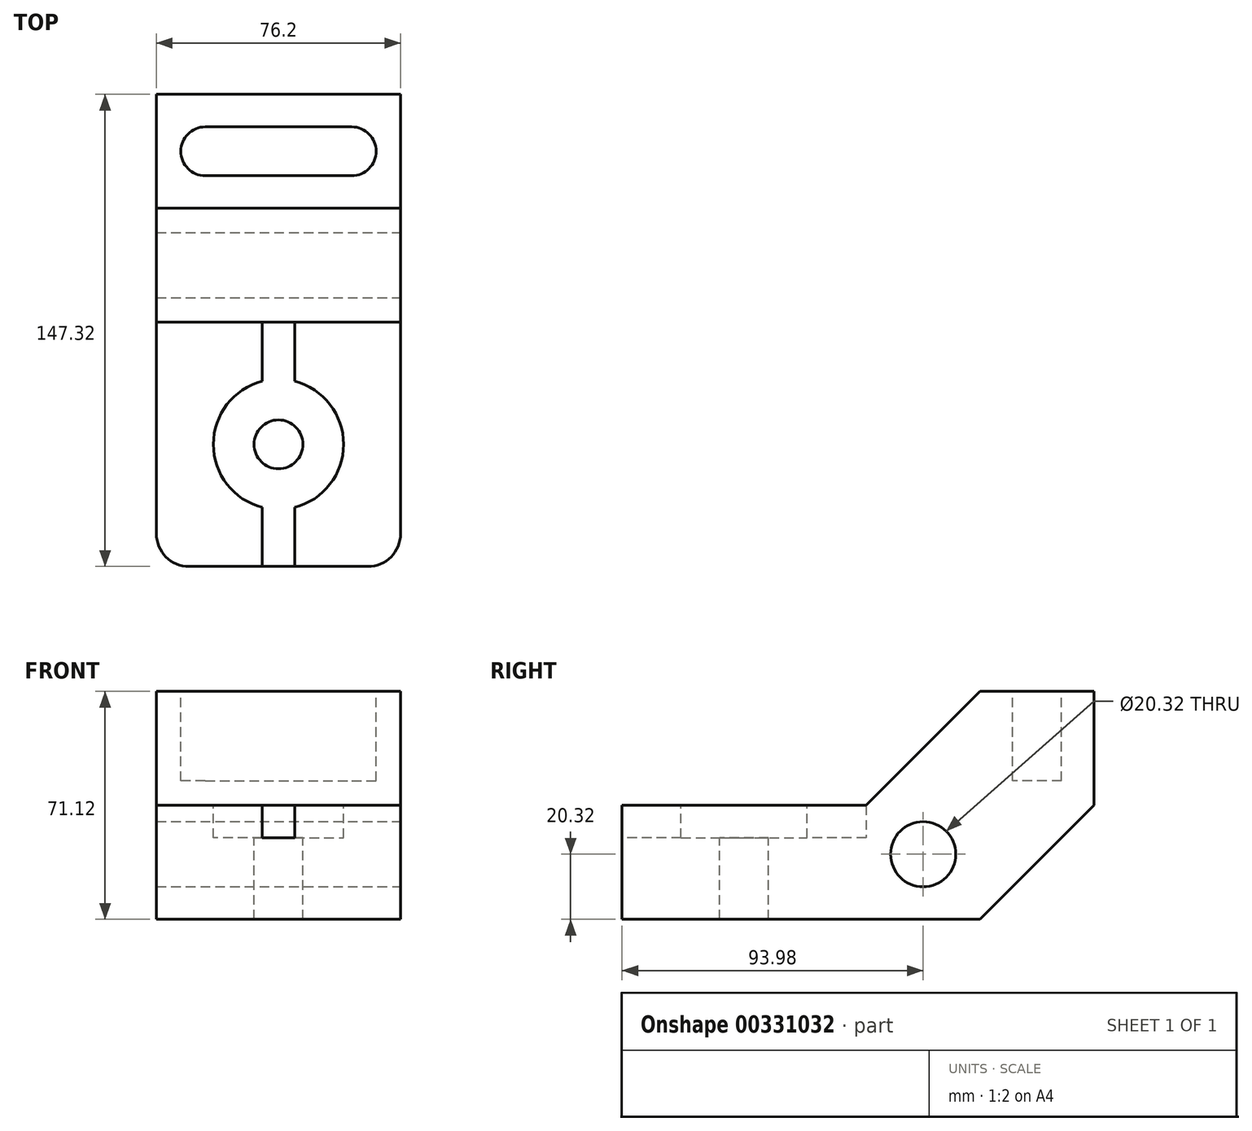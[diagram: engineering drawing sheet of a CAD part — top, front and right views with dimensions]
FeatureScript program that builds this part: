
annotation { "Feature Type Name" : "Feature", "Feature Type Description" : "" }
export const myFeature = defineFeature(function(context is Context, id is Id, definition is map)
    precondition{}
    {
        {
            var Q0;
            Q0=qCreatedBy(makeId("Right.planeOp"),FACE);
            var sketch = newSketch(context, id + "F0", { "sketchPlane" : qUnion([Q0])});
            skLineSegment(sketch, "E0", {"start": v(0, 0) * mm, "end": v(0, 35.56) * mm});
            skLineSegment(sketch, "E1", {"start": v(0, 35.56) * mm, "end": v(76.2, 35.56) * mm});
            skLineSegment(sketch, "E2", {"start": v(76.2, 35.56) * mm, "end": v(111.76, 71.12) * mm});
            skLineSegment(sketch, "E3", {"start": v(111.76, 71.12) * mm, "end": v(147.32, 71.12) * mm});
            skLineSegment(sketch, "E4", {"start": v(147.32, 71.12) * mm, "end": v(147.32, 35.56) * mm});
            skLineSegment(sketch, "E5", {"start": v(147.32, 35.56) * mm, "end": v(111.76, 0) * mm});
            skLineSegment(sketch, "E6", {"start": v(111.76, 0) * mm, "end": v(0, 0) * mm});
            skSolve(sketch);
        }
        {
            var Q0;
            Q0 = qSketchRegion(id + "F0", true);
            extrude(context, id + "F1", {"entities" : qUnion([Q0]), "depth" : 76.2 * mm});
        }
        {
            var Q0;
            Q0=makeQuery(id+"F1.opExtrude","SWEPT_FACE",FACE,{"disambiguationData":[OSD([sQuery(id+"F0.wireOp",EDGE,"E3")])]});
            var sketch = newSketch(context, id + "F2", { "sketchPlane" : qUnion([Q0])});
            skLineSegment(sketch, "E7", {"start": v(15.24, 129.54) * mm, "end": v(60.96, 129.54) * mm, "construction": true});
            skArc(sketch, "E8.0.startCap", {"start": v(15.24, 121.92) * mm, "mid": v(7.62, 129.54) * mm, "end": v(15.24, 137.16) * mm});
            skArc(sketch, "E8.0.endCap", {"start": v(60.96, 137.16) * mm, "mid": v(68.58, 129.54) * mm, "end": v(60.96, 121.92) * mm});
            skLineSegment(sketch, "E8.0.left", {"start": v(15.24, 137.16) * mm, "end": v(60.96, 137.16) * mm});
            skLineSegment(sketch, "E8.0.right", {"start": v(15.24, 121.92) * mm, "end": v(60.96, 121.92) * mm});
            skSolve(sketch);
        }
        {
            var Q0;
            Q0 = qSketchRegion(id + "F2", true);
            extrude(context, id + "F3", {"entities" : qUnion([Q0]), "operationType" : NewBodyOperationType.REMOVE, "oppositeDirection" : true, "depth" : 27.94 * mm});
        }
        {
            var Q0;
            Q0=makeQuery(id+"F1.opExtrude","CAP_FACE",FACE,{"disambiguationData":[OSD([sQuery(id+"F0.wireOp",EDGE,"E0"),sQuery(id+"F0.wireOp",EDGE,"E1"),sQuery(id+"F0.wireOp",EDGE,"E2"),sQuery(id+"F0.wireOp",EDGE,"E3"),sQuery(id+"F0.wireOp",EDGE,"E4"),sQuery(id+"F0.wireOp",EDGE,"E5"),sQuery(id+"F0.wireOp",EDGE,"E6")])],"isStart":false});
            var sketch = newSketch(context, id + "F4", { "sketchPlane" : qUnion([Q0])});
            skCircle(sketch, "E9", {"center": v(93.98, 20.32) * mm, "radius": 10.16 * mm});
            skSolve(sketch);
        }
        {
            var Q0;
            Q0 = qSketchRegion(id + "F4", true);
            extrude(context, id + "F5", {"entities" : qUnion([Q0]), "operationType" : NewBodyOperationType.REMOVE, "endBound" : BoundingType.THROUGH_ALL, "oppositeDirection" : true, "depth" : 25.4 * mm});
        }
        {
            var Q0;
            Q0=makeQuery(id+"F1.opExtrude","SWEPT_FACE",FACE,{"disambiguationData":[OSD([sQuery(id+"F0.wireOp",EDGE,"E1")])]});
            var sketch = newSketch(context, id + "F6", { "sketchPlane" : qUnion([Q0])});
            skPoint(sketch, "E10", {"position": v(38.1, 38.1) * mm});
            skPoint(sketch, "E10.positionSnap0", {"position": v(38.1, 76.2) * mm});
            skSolve(sketch);
        }
        {
            var Q0;
            Q0=sQuery(id+"F6.wireOp",VERTEX,"E10");
            var Q1;
            Q1=makeQuery(id+"F1.opExtrude","SWEPT_BODY",BODY,{"disambiguationData":[OSD([sQuery(id+"F0.wireOp",EDGE,"E0"),sQuery(id+"F0.wireOp",EDGE,"E1"),sQuery(id+"F0.wireOp",EDGE,"E2"),sQuery(id+"F0.wireOp",EDGE,"E3"),sQuery(id+"F0.wireOp",EDGE,"E4"),sQuery(id+"F0.wireOp",EDGE,"E5"),sQuery(id+"F0.wireOp",EDGE,"E6")])]});
            hole(context, id + "F7", {"style" : HoleStyle.C_BORE, "endStyle" : HoleEndStyle.THROUGH, "holeDiameter" : 15.24 * mm, "cBoreDiameter" : 40.64 * mm, "cBoreDepth" : 10.16 * mm, "tappedDepth" : 12.7 * mm, "tapClearance" : 3, "locations" : qUnion([Q0]), "scope" : qUnion([Q1])});
        }
        {
            var Q0;
            Q0=makeQuery(id+"F1.opExtrude","SWEPT_FACE",FACE,{"disambiguationData":[OSD([sQuery(id+"F0.wireOp",EDGE,"E0")])]});
            var sketch = newSketch(context, id + "F8", { "sketchPlane" : qUnion([Q0])});
            skLineSegment(sketch, "E11.bottom", {"start": v(33.02, 35.56) * mm, "end": v(43.18, 35.56) * mm});
            skLineSegment(sketch, "E11.top", {"start": v(33.02, 25.4) * mm, "end": v(43.18, 25.4) * mm});
            skLineSegment(sketch, "E11.left", {"start": v(33.02, 35.56) * mm, "end": v(33.02, 25.4) * mm});
            skLineSegment(sketch, "E11.right", {"start": v(43.18, 35.56) * mm, "end": v(43.18, 25.4) * mm});
            skSolve(sketch);
        }
        {
            var Q0;
            Q0 = qSketchRegion(id + "F8", true);
            extrude(context, id + "F9", {"entities" : qUnion([Q0]), "operationType" : NewBodyOperationType.REMOVE, "oppositeDirection" : true, "depth" : 76.2 * mm});
        }
        {
            var Q0;
            Q0=makeQuery(id+"F1.opExtrude","CAP_EDGE",EDGE,{"disambiguationData":[OSD([sQuery(id+"F0.wireOp",EDGE,"E0")])],"isStart":false});
            var Q1;
            Q1=makeQuery(id+"F1.opExtrude","CAP_EDGE",EDGE,{"disambiguationData":[OSD([sQuery(id+"F0.wireOp",EDGE,"E0")])],"isStart":true});
            fillet(context, id + "F10", {"entities" : qUnion([Q0, Q1]), "radius" : 10.16 * mm, "tangentPropagation" : true, "allowEdgeOverflow" : false});
        }
    });
